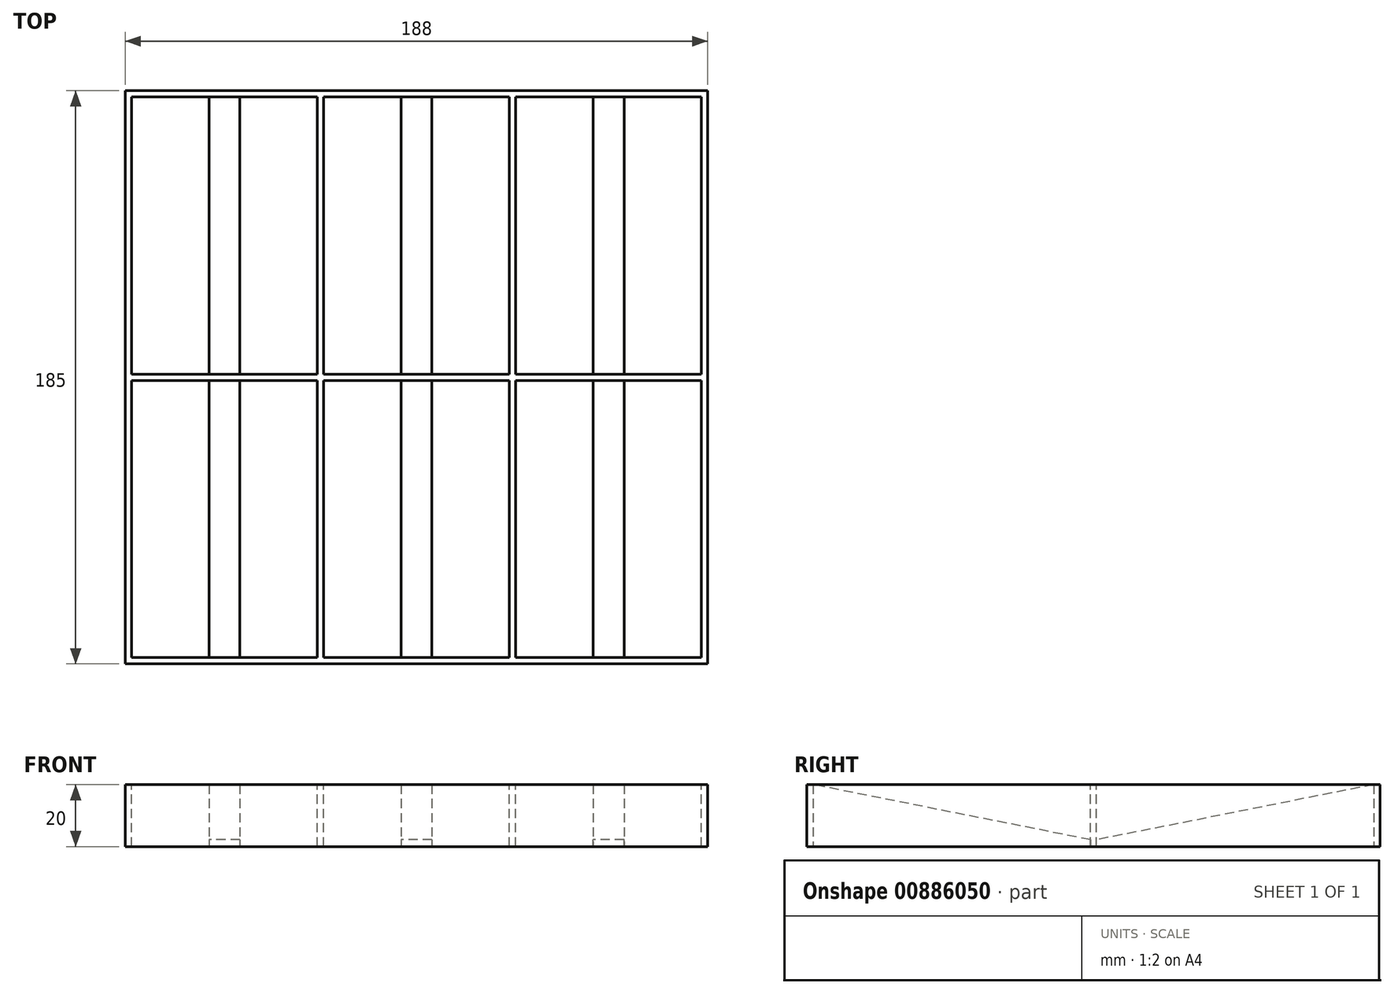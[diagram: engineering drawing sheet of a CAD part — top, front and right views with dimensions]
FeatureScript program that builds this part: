
annotation { "Feature Type Name" : "Feature", "Feature Type Description" : "" }
export const myFeature = defineFeature(function(context is Context, id is Id, definition is map)
    precondition{}
    {
        {
            var Q0;
            Q0=qCreatedBy(makeId("Top.planeOp"),FACE);
            var sketch = newSketch(context, id + "F0", { "sketchPlane" : qUnion([Q0])});
            skLineSegment(sketch, "E0.bottom", {"start": v(-94, -92.5) * mm, "end": v(94, -92.5) * mm});
            skLineSegment(sketch, "E0.top", {"start": v(-94, 92.5) * mm, "end": v(94, 92.5) * mm});
            skLineSegment(sketch, "E0.left", {"start": v(-94, -92.5) * mm, "end": v(-94, 92.5) * mm});
            skLineSegment(sketch, "E0.right", {"start": v(94, -92.5) * mm, "end": v(94, 92.5) * mm});
            skPoint(sketch, "E0.middle", {"position": v(0, 0) * mm});
            skSolve(sketch);
        }
        {
            var Q0;
            Q0 = qSketchRegion(id + "F0", true);
            extrude(context, id + "F1", {"entities" : qUnion([Q0]), "depth" : 20 * mm, "offsetDistance" : 25 * mm});
        }
        {
            var Q0;
            Q0=makeQuery(id+"F1.opExtrude","CAP_FACE",FACE,{"disambiguationData":[OSD([sQuery(id+"F0.wireOp",EDGE,"E0.bottom"),sQuery(id+"F0.wireOp",EDGE,"E0.top"),sQuery(id+"F0.wireOp",EDGE,"E0.left"),sQuery(id+"F0.wireOp",EDGE,"E0.right")])],"isStart":false});
            var sketch = newSketch(context, id + "F2", { "sketchPlane" : qUnion([Q0])});
            skLineSegment(sketch, "E1.bottom", {"start": v(92, 90.5) * mm, "end": v(32, 90.5) * mm});
            skLineSegment(sketch, "E1.top", {"start": v(92, 1) * mm, "end": v(32, 1) * mm});
            skLineSegment(sketch, "E1.left", {"start": v(92, 90.5) * mm, "end": v(92, 1) * mm});
            skLineSegment(sketch, "E1.right", {"start": v(32, 90.5) * mm, "end": v(32, 1) * mm});
            skLineSegment(sketch, "E2.bottom", {"start": v(30, 90.5) * mm, "end": v(-30, 90.5) * mm});
            skLineSegment(sketch, "E2.top", {"start": v(30, 1) * mm, "end": v(-30, 1) * mm});
            skLineSegment(sketch, "E2.left", {"start": v(30, 90.5) * mm, "end": v(30, 1) * mm});
            skLineSegment(sketch, "E2.right", {"start": v(-30, 90.5) * mm, "end": v(-30, 1) * mm});
            skLineSegment(sketch, "E3.bottom", {"start": v(-32, 90.5) * mm, "end": v(-92, 90.5) * mm});
            skLineSegment(sketch, "E3.top", {"start": v(-32, 1) * mm, "end": v(-92, 1) * mm});
            skLineSegment(sketch, "E3.left", {"start": v(-32, 90.5) * mm, "end": v(-32, 1) * mm});
            skLineSegment(sketch, "E3.right", {"start": v(-92, 90.5) * mm, "end": v(-92, 1) * mm});
            skLineSegment(sketch, "E4.top", {"start": v(92, -90.5) * mm, "end": v(32, -90.5) * mm});
            skLineSegment(sketch, "E4.left", {"start": v(92, -1) * mm, "end": v(92, -90.5) * mm});
            skLineSegment(sketch, "E4.right", {"start": v(32, -1) * mm, "end": v(32, -90.5) * mm});
            skLineSegment(sketch, "E5.bottom", {"start": v(30, -1) * mm, "end": v(-30, -1) * mm});
            skLineSegment(sketch, "E5.top", {"start": v(30, -90.5) * mm, "end": v(-30, -90.5) * mm});
            skLineSegment(sketch, "E5.left", {"start": v(30, -1) * mm, "end": v(30, -90.5) * mm});
            skLineSegment(sketch, "E5.right", {"start": v(-30, -1) * mm, "end": v(-30, -90.5) * mm});
            skLineSegment(sketch, "E6.bottom", {"start": v(-32, -1) * mm, "end": v(-92, -1) * mm});
            skLineSegment(sketch, "E6.top", {"start": v(-32, -90.5) * mm, "end": v(-92, -90.5) * mm});
            skLineSegment(sketch, "E6.left", {"start": v(-32, -1) * mm, "end": v(-32, -90.5) * mm});
            skLineSegment(sketch, "E6.right", {"start": v(-92, -1) * mm, "end": v(-92, -90.5) * mm});
            skLineSegment(sketch, "E7", {"start": v(32, -1) * mm, "end": v(92, -1) * mm});
            skSolve(sketch);
        }
        {
            var Q0;
            Q0 = qSketchRegion(id + "F2", true);
            extrude(context, id + "F3", {"entities" : qUnion([Q0]), "operationType" : NewBodyOperationType.REMOVE, "oppositeDirection" : true, "depth" : 25 * mm, "offsetDistance" : 25 * mm});
        }
        {
            var Q0;
            Q0=makeQuery(id+"F3.boolean.opBoolean","COPY",FACE,{"derivedFrom":makeQuery(id+"F3.opExtrude","SWEPT_FACE",FACE,{"disambiguationData":[OSD([sQuery(id+"F2.wireOp",EDGE,"E5.top")])]})});
            var sketch = newSketch(context, id + "F4", { "sketchPlane" : qUnion([Q0])});
            skLineSegment(sketch, "E8.bottom", {"start": v(-5, 20) * mm, "end": v(5, 20) * mm});
            skLineSegment(sketch, "E8.top", {"start": v(-5, 0) * mm, "end": v(5, 0) * mm});
            skLineSegment(sketch, "E8.left", {"start": v(-5, 20) * mm, "end": v(-5, 0) * mm});
            skLineSegment(sketch, "E8.right", {"start": v(5, 20) * mm, "end": v(5, 0) * mm});
            skLineSegment(sketch, "E9.bottom", {"start": v(57, 20) * mm, "end": v(67, 20) * mm});
            skLineSegment(sketch, "E9.top", {"start": v(57, 0) * mm, "end": v(67, 0) * mm});
            skLineSegment(sketch, "E9.left", {"start": v(57, 20) * mm, "end": v(57, 0) * mm});
            skLineSegment(sketch, "E9.right", {"start": v(67, 20) * mm, "end": v(67, 0) * mm});
            skLineSegment(sketch, "E10.bottom", {"start": v(-67, 20) * mm, "end": v(-57, 20) * mm});
            skLineSegment(sketch, "E10.top", {"start": v(-67, 0) * mm, "end": v(-57, 0) * mm});
            skLineSegment(sketch, "E10.left", {"start": v(-67, 20) * mm, "end": v(-67, 0) * mm});
            skLineSegment(sketch, "E10.right", {"start": v(-57, 20) * mm, "end": v(-57, 0) * mm});
            skSolve(sketch);
        }
        {
            var Q0;
            Q0=qCreatedBy(makeId("Front.planeOp"),FACE);
            var sketch = newSketch(context, id + "F5", { "sketchPlane" : qUnion([Q0])});
            skLineSegment(sketch, "E11.bottom", {"start": v(-57, 2) * mm, "end": v(-67, 2) * mm});
            skLineSegment(sketch, "E11.top", {"start": v(-57, 0) * mm, "end": v(-67, 0) * mm});
            skLineSegment(sketch, "E11.left", {"start": v(-57, 2) * mm, "end": v(-57, 0) * mm});
            skLineSegment(sketch, "E11.right", {"start": v(-67, 2) * mm, "end": v(-67, 0) * mm});
            skLineSegment(sketch, "E12.bottom", {"start": v(5, 2) * mm, "end": v(-5, 2) * mm});
            skLineSegment(sketch, "E12.top", {"start": v(5, 0) * mm, "end": v(-5, 0) * mm});
            skLineSegment(sketch, "E12.left", {"start": v(5, 2) * mm, "end": v(5, 0) * mm});
            skLineSegment(sketch, "E12.right", {"start": v(-5, 2) * mm, "end": v(-5, 0) * mm});
            skLineSegment(sketch, "E13.bottom", {"start": v(67, 2) * mm, "end": v(57, 2) * mm});
            skLineSegment(sketch, "E13.top", {"start": v(67, 0) * mm, "end": v(57, 0) * mm});
            skLineSegment(sketch, "E13.left", {"start": v(67, 2) * mm, "end": v(67, 0) * mm});
            skLineSegment(sketch, "E13.right", {"start": v(57, 2) * mm, "end": v(57, 0) * mm});
            skSolve(sketch);
        }
        {
            var Q0;
            Q0=makeQuery(id+"F3.boolean.opBoolean","COPY",FACE,{"derivedFrom":makeQuery(id+"F3.opExtrude","SWEPT_FACE",FACE,{"disambiguationData":[OSD([sQuery(id+"F2.wireOp",EDGE,"E3.bottom")])]})});
            var sketch = newSketch(context, id + "F6", { "sketchPlane" : qUnion([Q0])});
            skLineSegment(sketch, "E14.bottom", {"start": v(-67, 20) * mm, "end": v(-57, 20) * mm});
            skLineSegment(sketch, "E14.top", {"start": v(-67, 0) * mm, "end": v(-57, 0) * mm});
            skLineSegment(sketch, "E14.left", {"start": v(-67, 20) * mm, "end": v(-67, 0) * mm});
            skLineSegment(sketch, "E14.right", {"start": v(-57, 20) * mm, "end": v(-57, 0) * mm});
            skLineSegment(sketch, "E15.bottom", {"start": v(-5, 20) * mm, "end": v(5, 20) * mm});
            skLineSegment(sketch, "E15.top", {"start": v(-5, 0) * mm, "end": v(5, 0) * mm});
            skLineSegment(sketch, "E15.left", {"start": v(-5, 20) * mm, "end": v(-5, 0) * mm});
            skLineSegment(sketch, "E15.right", {"start": v(5, 20) * mm, "end": v(5, 0) * mm});
            skLineSegment(sketch, "E16.bottom", {"start": v(57, 20) * mm, "end": v(67, 20) * mm});
            skLineSegment(sketch, "E16.top", {"start": v(57, 0) * mm, "end": v(67, 0) * mm});
            skLineSegment(sketch, "E16.left", {"start": v(57, 20) * mm, "end": v(57, 0) * mm});
            skLineSegment(sketch, "E16.right", {"start": v(67, 20) * mm, "end": v(67, 0) * mm});
            skSolve(sketch);
        }
        {
            var Q0;
            Q0=qCreatedBy(makeId("Right.planeOp"),FACE);
            var sketch = newSketch(context, id + "F7", { "sketchPlane" : qUnion([Q0])});
            skLineSegment(sketch, "E17", {"start": v(90.5, 20) * mm, "end": v(0, 2) * mm});
            skLineSegment(sketch, "E18", {"start": v(0, 2) * mm, "end": v(-90.5, 20) * mm});
            skSolve(sketch);
        }
        {
            var Q0;
            Q0=sQuery(id+"F7.wireOp",EDGE,"E17");
            var Q1;
            Q1=sQuery(id+"F7.wireOp",EDGE,"E18");
            var Q3;
            Q3=makeQuery(id+"F6.imprint","IMPRINT",FACE,{"disambiguationData":[TD([[makeQuery(id+"F6.imprint","IMPRINT",EDGE,{"derivedFrom":sQuery(id+"F6.wireOp",EDGE,"E14.bottom")}),1.0]])]});
            var Q4;
            Q4=makeQuery(id+"F5.imprint","IMPRINT",FACE,{"disambiguationData":[TD([[makeQuery(id+"F5.imprint","IMPRINT",EDGE,{"derivedFrom":sQuery(id+"F5.wireOp",EDGE,"E11.bottom")}),1.0]])]});
            loft(context, id + "F8", {"operationType" : NewBodyOperationType.ADD, "spine" : qUnion([Q0, Q1]), "sheetProfilesArray" : [{ "sheetProfileEntities" : qUnion([Q3]) }, { "sheetProfileEntities" : qUnion([Q4]) }]});
        }
        {
            var Q1;
            Q1=makeQuery(id+"F6.imprint","IMPRINT",FACE,{"disambiguationData":[TD([[makeQuery(id+"F6.imprint","IMPRINT",EDGE,{"derivedFrom":sQuery(id+"F6.wireOp",EDGE,"E15.bottom")}),-1.0]])]});
            var Q2;
            Q2=makeQuery(id+"F5.imprint","IMPRINT",FACE,{"disambiguationData":[TD([[makeQuery(id+"F5.imprint","IMPRINT",EDGE,{"derivedFrom":sQuery(id+"F5.wireOp",EDGE,"E12.bottom")}),1.0]])]});
            loft(context, id + "F9", {"operationType" : NewBodyOperationType.ADD, "sheetProfilesArray" : [{ "sheetProfileEntities" : qUnion([Q1]) }, { "sheetProfileEntities" : qUnion([Q2]) }]});
        }
        {
            var Q1;
            Q1=makeQuery(id+"F6.imprint","IMPRINT",FACE,{"disambiguationData":[TD([[makeQuery(id+"F6.imprint","IMPRINT",EDGE,{"derivedFrom":sQuery(id+"F6.wireOp",EDGE,"E16.bottom")}),-1.0]])]});
            var Q2;
            Q2=makeQuery(id+"F5.imprint","IMPRINT",FACE,{"disambiguationData":[TD([[makeQuery(id+"F5.imprint","IMPRINT",EDGE,{"derivedFrom":sQuery(id+"F5.wireOp",EDGE,"E13.bottom")}),1.0]])]});
            loft(context, id + "F10", {"operationType" : NewBodyOperationType.ADD, "sheetProfilesArray" : [{ "sheetProfileEntities" : qUnion([Q1]) }, { "sheetProfileEntities" : qUnion([Q2]) }]});
        }
        {
            var Q1;
            Q1=makeQuery(id+"F5.imprint","IMPRINT",FACE,{"disambiguationData":[TD([[makeQuery(id+"F5.imprint","IMPRINT",EDGE,{"derivedFrom":sQuery(id+"F5.wireOp",EDGE,"E13.bottom")}),1.0]])]});
            var Q2;
            Q2=makeQuery(id+"F4.imprint","IMPRINT",FACE,{"disambiguationData":[TD([[makeQuery(id+"F4.imprint","IMPRINT",EDGE,{"derivedFrom":sQuery(id+"F4.wireOp",EDGE,"E10.bottom")}),-1.0]])]});
            loft(context, id + "F11", {"operationType" : NewBodyOperationType.ADD, "sheetProfilesArray" : [{ "sheetProfileEntities" : qUnion([Q1]) }, { "sheetProfileEntities" : qUnion([Q2]) }]});
        }
        {
            var Q1;
            Q1=makeQuery(id+"F4.imprint","IMPRINT",FACE,{"disambiguationData":[TD([[makeQuery(id+"F4.imprint","IMPRINT",EDGE,{"derivedFrom":sQuery(id+"F4.wireOp",EDGE,"E8.bottom")}),-1.0]])]});
            var Q2;
            Q2=makeQuery(id+"F5.imprint","IMPRINT",FACE,{"disambiguationData":[TD([[makeQuery(id+"F5.imprint","IMPRINT",EDGE,{"derivedFrom":sQuery(id+"F5.wireOp",EDGE,"E12.bottom")}),1.0]])]});
            loft(context, id + "F12", {"operationType" : NewBodyOperationType.ADD, "sheetProfilesArray" : [{ "sheetProfileEntities" : qUnion([Q1]) }, { "sheetProfileEntities" : qUnion([Q2]) }]});
        }
        {
            var Q1;
            Q1=makeQuery(id+"F4.imprint","IMPRINT",FACE,{"disambiguationData":[TD([[makeQuery(id+"F4.imprint","IMPRINT",EDGE,{"derivedFrom":sQuery(id+"F4.wireOp",EDGE,"E9.bottom")}),-1.0]])]});
            var Q2;
            Q2=makeQuery(id+"F5.imprint","IMPRINT",FACE,{"disambiguationData":[TD([[makeQuery(id+"F5.imprint","IMPRINT",EDGE,{"derivedFrom":sQuery(id+"F5.wireOp",EDGE,"E11.bottom")}),1.0]])]});
            loft(context, id + "F13", {"operationType" : NewBodyOperationType.ADD, "sheetProfilesArray" : [{ "sheetProfileEntities" : qUnion([Q1]) }, { "sheetProfileEntities" : qUnion([Q2]) }]});
        }
    });
